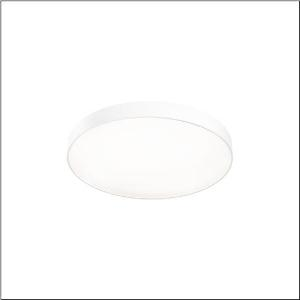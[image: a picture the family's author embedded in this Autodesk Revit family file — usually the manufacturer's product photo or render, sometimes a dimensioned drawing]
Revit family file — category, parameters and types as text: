
# Revit family: round_21_m_51mr36fd0421w
name_source: partatom
category: Lighting Fixtures
units: mm (PartAtom-declared; Revit-internal decimal feet)

## family parameters
Cut with Voids When Loaded = No
Host = Face
Light Source = No
Part Type = Normal
Room Calculation Point = No
Round Connector Dimension = Use Diameter
Shared = No

## types (1)
- Round 21 M (1 x LED, 7110 lm, 54.8 W, 4000K)
    Apparent Load = 55 VA
    CIE Flux Codes = 49 80 96 100 100
    Color Rendering = 80
    Color Temperature = 4000K
    Default Elevation = 1800 mm
    Description = Round 21 M, wall and ceiling luminaire, primary optical cover: cover, of PMMA, opal, light emission: direct distribution, primary light characteristic: symmetric, installation type: surface-mounted, suspended mounting, LED, rated luminous flux: 7.110lm, luminous efficacy: 130lm/W, light colour: 840, colour temperature: 4000K, with terminal, 5-pole, mains connection: 230V, AC, 50/60Hz, rated input power: 55W, housing, of aluminium, coated, white, diameter: 600mm, height: 62mm, protection rating (complete): IP40, insulation class (complete): insulation class I (protective earthing), certification: CE, impact resistance: IK04, permissible operating ambient temperature: -10..+35°C, packaging unit: 1 piece
    Height = 87 mm
    Lamp = 1 x LED
    Lamp Light Flux = 7110 lm
    Lamp Power = 54.8 W
    Lamp count = 1
    Length = 600 mm
    Luminous efficacy = 130 lm/W
    Manufacturer = Siteco
    ModVariant = No
    Model = 51MR36FD0421W
    Mounting Place = Ceiling
    Mounting Type = Surface mounted
    Number of Poles = 1
    OnlyDefault = Yes
    Power Factor = 1
    Product Name = Round 21 M
    Product group = wall and ceiling luminaire
    ProductGroupID = 302
    Protection Class = Protection class I
    Protection Degree = IP 40
    RLX_Detail_Level = 1
    RLX_Emergency_Light_Flux = 0 lm
    RLX_Emergency_Type = 0
    RLX_Emergency_Type_DB = No
    RlxData = <blob elided: 11689 chars, md5=53f60960>
    Socket = socket
    Standby Power = 0 W
    System Light Flux = 7110 lm
    System Power = 55 W
    Type Comments = Product without accessories
    Type Image = l_1258330.jpg
    URL = http://relux.com
    VarID = ---
    Voltage = 0 V
    Weight = 0.00 kg
    Width = 0 mm  [stored 0 ft]

note: [stored X ft] marks values corroborated as IEEE doubles in the binary element streams (Revit-internal decimal feet)

## geometry (parser evidence)
native form markers: Sweep x10
no freeform markers — native parametric forms only
